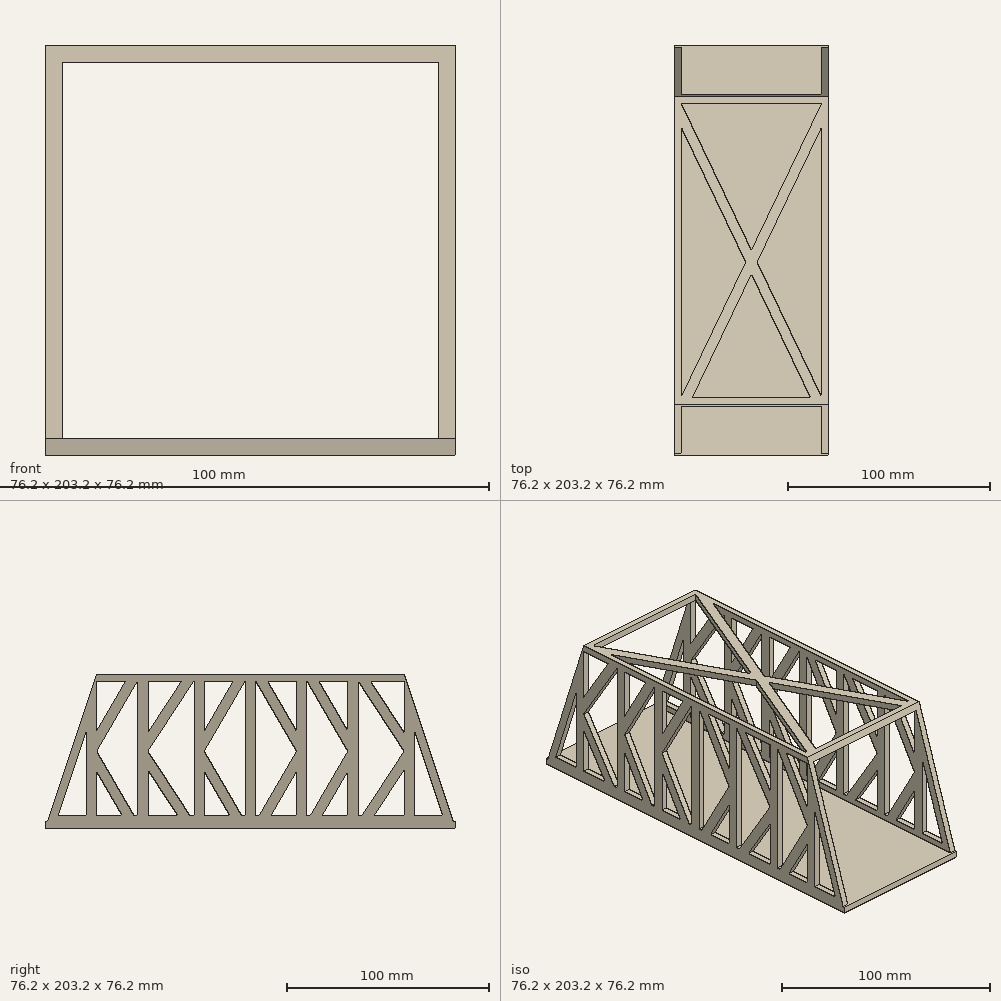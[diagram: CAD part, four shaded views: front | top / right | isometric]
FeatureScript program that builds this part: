
annotation { "Feature Type Name" : "Feature", "Feature Type Description" : "" }
export const myFeature = defineFeature(function(context is Context, id is Id, definition is map)
    precondition{}
    {
        {
            var Q0;
            Q0=qCreatedBy(makeId("Right.planeOp"),FACE);
            var sketch = newSketch(context, id + "F0", { "sketchPlane" : qUnion([Q0])});
            skLineSegment(sketch, "E0", {"start": v(-101.6, -38.1) * mm, "end": v(101.6, -38.1) * mm});
            skLineSegment(sketch, "E1", {"start": v(-76.2, 38.1) * mm, "end": v(76.2, 38.1) * mm});
            skLineSegment(sketch, "E2", {"start": v(-76.2, 38.1) * mm, "end": v(-101.6, -38.1) * mm});
            skLineSegment(sketch, "E3", {"start": v(76.2, 38.1) * mm, "end": v(101.6, -38.1) * mm});
            skSolve(sketch);
        }
        {
            var Q0;
            Q0 = qSketchRegion(id + "F0", true);
            extrude(context, id + "F1", {"entities" : qUnion([Q0]), "endBound" : BoundingType.SYMMETRIC, "depth" : 76.2 * mm, "offsetDistance" : 25.4 * mm});
        }
        {
            var Q0;
            Q0=qCreatedBy(makeId("Front.planeOp"),FACE);
            var sketch = newSketch(context, id + "F2", { "sketchPlane" : qUnion([Q0])});
            skLineSegment(sketch, "E4.bottom", {"start": v(34.92, -34.92) * mm, "end": v(-34.92, -34.93) * mm});
            skLineSegment(sketch, "E4.top", {"start": v(34.92, 34.93) * mm, "end": v(-34.92, 34.92) * mm});
            skLineSegment(sketch, "E4.left", {"start": v(-34.92, -34.92) * mm, "end": v(-34.92, 34.92) * mm});
            skLineSegment(sketch, "E4.right", {"start": v(34.92, -34.92) * mm, "end": v(34.92, 34.92) * mm});
            skPoint(sketch, "E4.middle", {"position": v(0, 0) * mm});
            skSolve(sketch);
        }
        {
            var Q0;
            Q0 = qSketchRegion(id + "F2", true);
            extrude(context, id + "F3", {"entities" : qUnion([Q0]), "operationType" : NewBodyOperationType.REMOVE, "endBound" : BoundingType.SYMMETRIC, "oppositeDirection" : true, "depth" : 254 * mm, "offsetDistance" : 25.4 * mm});
        }
        {
            var Q0;
            Q0=makeQuery(id+"F1.opExtrude","CAP_FACE",FACE,{"disambiguationData":[OSD([sQuery(id+"F0.wireOp",EDGE,"E0"),sQuery(id+"F0.wireOp",EDGE,"E1"),sQuery(id+"F0.wireOp",EDGE,"E2"),sQuery(id+"F0.wireOp",EDGE,"E3")])],"isStart":false});
            var sketch = newSketch(context, id + "F4", { "sketchPlane" : qUnion([Q0])});
            skLineSegment(sketch, "E5.bottom", {"start": v(76.2, -34.92) * mm, "end": v(-76.2, -34.92) * mm});
            skLineSegment(sketch, "E5.top", {"start": v(76.2, 34.92) * mm, "end": v(-76.2, 34.92) * mm});
            skLineSegment(sketch, "E5.left", {"start": v(76.2, -34.92) * mm, "end": v(76.2, 34.92) * mm});
            skLineSegment(sketch, "E5.right", {"start": v(-76.2, -34.92) * mm, "end": v(-76.2, 34.92) * mm});
            skPoint(sketch, "E5.middle", {"position": v(0, 0) * mm});
            skLineSegment(sketch, "E6.bottom", {"start": v(2.54, -34.92) * mm, "end": v(-2.54, -34.92) * mm});
            skLineSegment(sketch, "E6.top", {"start": v(2.54, 34.92) * mm, "end": v(-2.54, 34.92) * mm});
            skLineSegment(sketch, "E6.left", {"start": v(2.54, -34.93) * mm, "end": v(2.54, 34.93) * mm});
            skLineSegment(sketch, "E6.right", {"start": v(-2.54, -34.93) * mm, "end": v(-2.54, 34.93) * mm});
            skLineSegment(sketch, "E7.bottom", {"start": v(-50.8, -34.92) * mm, "end": v(-55.88, -34.92) * mm});
            skLineSegment(sketch, "E7.top", {"start": v(-50.8, 34.92) * mm, "end": v(-55.88, 34.92) * mm});
            skLineSegment(sketch, "E7.left", {"start": v(-50.8, -34.93) * mm, "end": v(-50.8, 34.93) * mm});
            skLineSegment(sketch, "E7.right", {"start": v(-55.88, -34.93) * mm, "end": v(-55.88, 34.93) * mm});
            skPoint(sketch, "E7.middle", {"position": v(-53.34, 0) * mm});
            skLineSegment(sketch, "E8.bottom", {"start": v(-22.86, -34.92) * mm, "end": v(-27.94, -34.92) * mm});
            skLineSegment(sketch, "E8.top", {"start": v(-22.86, 34.92) * mm, "end": v(-27.94, 34.92) * mm});
            skLineSegment(sketch, "E8.left", {"start": v(-22.86, -34.92) * mm, "end": v(-22.86, 34.92) * mm});
            skLineSegment(sketch, "E8.right", {"start": v(-27.94, -34.92) * mm, "end": v(-27.94, 34.92) * mm});
            skPoint(sketch, "E8.middle", {"position": v(-25.4, 0) * mm});
            skLineSegment(sketch, "E9.bottom", {"start": v(27.94, -34.92) * mm, "end": v(22.86, -34.92) * mm});
            skLineSegment(sketch, "E9.top", {"start": v(27.94, 34.92) * mm, "end": v(22.86, 34.92) * mm});
            skLineSegment(sketch, "E9.left", {"start": v(27.94, -34.92) * mm, "end": v(27.94, 34.92) * mm});
            skLineSegment(sketch, "E9.right", {"start": v(22.86, -34.93) * mm, "end": v(22.86, 34.92) * mm});
            skPoint(sketch, "E9.middle", {"position": v(25.4, 0) * mm});
            skLineSegment(sketch, "E10.bottom", {"start": v(53.34, -34.92) * mm, "end": v(48.26, -34.92) * mm});
            skLineSegment(sketch, "E10.top", {"start": v(53.34, 34.92) * mm, "end": v(48.26, 34.92) * mm});
            skLineSegment(sketch, "E10.left", {"start": v(53.34, -34.93) * mm, "end": v(53.34, 34.93) * mm});
            skLineSegment(sketch, "E10.right", {"start": v(48.26, -34.93) * mm, "end": v(48.26, 34.93) * mm});
            skPoint(sketch, "E10.middle", {"position": v(50.8, 0) * mm});
            skLineSegment(sketch, "E11", {"start": v(-55.88, 34.92) * mm, "end": v(-76.2, 0) * mm});
            skLineSegment(sketch, "E12", {"start": v(-76.2, 0) * mm, "end": v(-55.88, -34.92) * mm});
            skLineSegment(sketch, "E13", {"start": v(-27.94, 34.92) * mm, "end": v(-50.8, 0) * mm});
            skLineSegment(sketch, "E14", {"start": v(-50.8, 0) * mm, "end": v(-27.94, -34.92) * mm});
            skLineSegment(sketch, "E15", {"start": v(-2.54, 34.92) * mm, "end": v(-22.86, 0) * mm});
            skLineSegment(sketch, "E16", {"start": v(-22.86, 0) * mm, "end": v(-2.54, -34.92) * mm});
            skLineSegment(sketch, "E17", {"start": v(2.54, 34.92) * mm, "end": v(22.86, 0) * mm});
            skLineSegment(sketch, "E18", {"start": v(22.86, 0) * mm, "end": v(2.54, -34.92) * mm});
            skLineSegment(sketch, "E19", {"start": v(27.94, 34.93) * mm, "end": v(48.26, 0) * mm});
            skLineSegment(sketch, "E20", {"start": v(48.26, 0) * mm, "end": v(27.94, -34.93) * mm});
            skLineSegment(sketch, "E21", {"start": v(53.34, 34.92) * mm, "end": v(76.2, 0) * mm});
            skLineSegment(sketch, "E22", {"start": v(76.2, 0) * mm, "end": v(53.34, -34.92) * mm});
            skLineSegment(sketch, "E23", {"start": v(-76.2, -10.1) * mm, "end": v(-61.76, -34.93) * mm});
            skLineSegment(sketch, "E24", {"start": v(-34.01, 34.93) * mm, "end": v(-50.8, 9.28) * mm});
            skLineSegment(sketch, "E25", {"start": v(-50.8, -9.28) * mm, "end": v(-34.01, -34.93) * mm});
            skLineSegment(sketch, "E26", {"start": v(-8.42, 34.93) * mm, "end": v(-22.86, 10.1) * mm});
            skLineSegment(sketch, "E27", {"start": v(-22.86, -10.1) * mm, "end": v(-8.42, -34.93) * mm});
            skLineSegment(sketch, "E28", {"start": v(-61.76, 34.93) * mm, "end": v(-76.2, 10.1) * mm});
            skLineSegment(sketch, "E29", {"start": v(8.42, 34.93) * mm, "end": v(22.86, 10.1) * mm});
            skLineSegment(sketch, "E30", {"start": v(22.86, -10.1) * mm, "end": v(8.42, -34.93) * mm});
            skLineSegment(sketch, "E31", {"start": v(33.82, 34.93) * mm, "end": v(48.26, 10.1) * mm});
            skLineSegment(sketch, "E32", {"start": v(48.26, -10.1) * mm, "end": v(33.82, -34.93) * mm});
            skLineSegment(sketch, "E33", {"start": v(59.41, 34.93) * mm, "end": v(76.2, 9.28) * mm});
            skLineSegment(sketch, "E34", {"start": v(76.2, -9.28) * mm, "end": v(59.41, -34.93) * mm});
            skLineSegment(sketch, "E35", {"start": v(-81.28, -34.93) * mm, "end": v(-81.28, 10.1) * mm});
            skLineSegment(sketch, "E36", {"start": v(-81.28, 10.1) * mm, "end": v(-96.29, -34.93) * mm});
            skLineSegment(sketch, "E37", {"start": v(-96.29, -34.92) * mm, "end": v(-81.28, -34.92) * mm});
            skLineSegment(sketch, "E38.MirrorCS", {"start": v(81.28, -34.93) * mm, "end": v(81.28, 10.1) * mm});
            skLineSegment(sketch, "E39.MirrorCS", {"start": v(81.28, 10.1) * mm, "end": v(96.29, -34.93) * mm});
            skLineSegment(sketch, "E40.MirrorCS", {"start": v(96.29, -34.92) * mm, "end": v(81.28, -34.92) * mm});
            skSolve(sketch);
        }
        {
            var Q0;
            Q0=makeQuery(id+"F4.imprint","IMPRINT",FACE,{"disambiguationData":[TD([[makeQuery(id+"F4.imprint","IMPRINT",EDGE,{"derivedFrom":sQuery(id+"F4.wireOp",EDGE,"E35")}),1.0]])]});
            var Q1;
            {var subQ3=sQuery(id+"F4.wireOp",EDGE,"E28");Q1=makeQuery(id+"F4.imprint","IMPRINT",FACE,{"disambiguationData":[TD([[makeQuery(id+"F4.imprint","IMPRINT",EDGE,{"derivedFrom":subQ3}),-1.0]])]});}
            var Q2;
            Q2=makeQuery(id+"F4.imprint","IMPRINT",FACE,{"disambiguationData":[TD([[makeQuery(id+"F4.imprint","IMPRINT",EDGE,{"derivedFrom":sQuery(id+"F4.wireOp",EDGE,"E7.right")}),1.0]])]});
            var Q3;
            {var subQ3=sQuery(id+"F4.wireOp",EDGE,"E23");Q3=makeQuery(id+"F4.imprint","IMPRINT",FACE,{"disambiguationData":[TD([[makeQuery(id+"F4.imprint","IMPRINT",EDGE,{"derivedFrom":subQ3}),-1.0]])]});}
            var Q4;
            {var subQ3=sQuery(id+"F4.wireOp",EDGE,"E24");Q4=makeQuery(id+"F4.imprint","IMPRINT",FACE,{"disambiguationData":[TD([[makeQuery(id+"F4.imprint","IMPRINT",EDGE,{"derivedFrom":subQ3}),-1.0]])]});}
            var Q5;
            Q5=makeQuery(id+"F4.imprint","IMPRINT",FACE,{"disambiguationData":[TD([[makeQuery(id+"F4.imprint","IMPRINT",EDGE,{"derivedFrom":sQuery(id+"F4.wireOp",EDGE,"E8.right")}),1.0]])]});
            var Q6;
            {var subQ3=sQuery(id+"F4.wireOp",EDGE,"E25");Q6=makeQuery(id+"F4.imprint","IMPRINT",FACE,{"disambiguationData":[TD([[makeQuery(id+"F4.imprint","IMPRINT",EDGE,{"derivedFrom":subQ3}),-1.0]])]});}
            var Q7;
            {var subQ3=sQuery(id+"F4.wireOp",EDGE,"E26");Q7=makeQuery(id+"F4.imprint","IMPRINT",FACE,{"disambiguationData":[TD([[makeQuery(id+"F4.imprint","IMPRINT",EDGE,{"derivedFrom":subQ3}),-1.0]])]});}
            var Q8;
            Q8=makeQuery(id+"F4.imprint","IMPRINT",FACE,{"disambiguationData":[TD([[makeQuery(id+"F4.imprint","IMPRINT",EDGE,{"derivedFrom":sQuery(id+"F4.wireOp",EDGE,"E6.right")}),1.0]])]});
            var Q9;
            {var subQ3=sQuery(id+"F4.wireOp",EDGE,"E27");Q9=makeQuery(id+"F4.imprint","IMPRINT",FACE,{"disambiguationData":[TD([[makeQuery(id+"F4.imprint","IMPRINT",EDGE,{"derivedFrom":subQ3}),-1.0]])]});}
            var Q10;
            Q10=makeQuery(id+"F4.imprint","IMPRINT",FACE,{"disambiguationData":[TD([[makeQuery(id+"F4.imprint","IMPRINT",EDGE,{"derivedFrom":sQuery(id+"F4.wireOp",EDGE,"E6.left")}),-1.0]])]});
            var Q11;
            {var subQ3=sQuery(id+"F4.wireOp",EDGE,"E29");Q11=makeQuery(id+"F4.imprint","IMPRINT",FACE,{"disambiguationData":[TD([[makeQuery(id+"F4.imprint","IMPRINT",EDGE,{"derivedFrom":subQ3}),1.0]])]});}
            var Q12;
            Q12=makeQuery(id+"F4.imprint","IMPRINT",FACE,{"disambiguationData":[TD([[makeQuery(id+"F4.imprint","IMPRINT",EDGE,{"derivedFrom":sQuery(id+"F4.wireOp",EDGE,"E9.left")}),-1.0]])]});
            var Q13;
            {var subQ3=sQuery(id+"F4.wireOp",EDGE,"E30");Q13=makeQuery(id+"F4.imprint","IMPRINT",FACE,{"disambiguationData":[TD([[makeQuery(id+"F4.imprint","IMPRINT",EDGE,{"derivedFrom":subQ3}),1.0]])]});}
            var Q14;
            {var subQ3=sQuery(id+"F4.wireOp",EDGE,"E31");Q14=makeQuery(id+"F4.imprint","IMPRINT",FACE,{"disambiguationData":[TD([[makeQuery(id+"F4.imprint","IMPRINT",EDGE,{"derivedFrom":subQ3}),1.0]])]});}
            var Q15;
            {var subQ3=sQuery(id+"F4.wireOp",EDGE,"E32");Q15=makeQuery(id+"F4.imprint","IMPRINT",FACE,{"disambiguationData":[TD([[makeQuery(id+"F4.imprint","IMPRINT",EDGE,{"derivedFrom":subQ3}),1.0]])]});}
            var Q16;
            Q16=makeQuery(id+"F4.imprint","IMPRINT",FACE,{"disambiguationData":[TD([[makeQuery(id+"F4.imprint","IMPRINT",EDGE,{"derivedFrom":sQuery(id+"F4.wireOp",EDGE,"E10.left")}),-1.0]])]});
            var Q17;
            {var subQ3=sQuery(id+"F4.wireOp",EDGE,"E33");Q17=makeQuery(id+"F4.imprint","IMPRINT",FACE,{"disambiguationData":[TD([[makeQuery(id+"F4.imprint","IMPRINT",EDGE,{"derivedFrom":subQ3}),1.0]])]});}
            var Q18;
            {var subQ3=sQuery(id+"F4.wireOp",EDGE,"E34");Q18=makeQuery(id+"F4.imprint","IMPRINT",FACE,{"disambiguationData":[TD([[makeQuery(id+"F4.imprint","IMPRINT",EDGE,{"derivedFrom":subQ3}),1.0]])]});}
            var Q19;
            Q19=makeQuery(id+"F4.imprint","IMPRINT",FACE,{"disambiguationData":[TD([[makeQuery(id+"F4.imprint","IMPRINT",EDGE,{"derivedFrom":sQuery(id+"F4.wireOp",EDGE,"E38.MirrorCS")}),-1.0]])]});
            extrude(context, id + "F5", {"entities" : qUnion([Q0, Q1, Q2, Q3, Q4, Q5, Q6, Q7, Q8, Q9, Q10, Q11, Q12, Q13, Q14, Q15, Q16, Q17, Q18, Q19]), "operationType" : NewBodyOperationType.REMOVE, "oppositeDirection" : true, "depth" : 76.2 * mm, "offsetDistance" : 25.4 * mm});
        }
        {
            var Q0;
            Q0=makeQuery(id+"F1.opExtrude","CAP_FACE",FACE,{"disambiguationData":[OSD([sQuery(id+"F0.wireOp",EDGE,"E0"),sQuery(id+"F0.wireOp",EDGE,"E1"),sQuery(id+"F0.wireOp",EDGE,"E2"),sQuery(id+"F0.wireOp",EDGE,"E3")])],"isStart":false});
            var sketch = newSketch(context, id + "F6", { "sketchPlane" : qUnion([Q0])});
            skLineSegment(sketch, "E41.bottom", {"start": v(-96.29, -34.93) * mm, "end": v(-101.6, -34.93) * mm});
            skLineSegment(sketch, "E41.top", {"start": v(-96.29, -38.1) * mm, "end": v(-101.6, -38.1) * mm});
            skLineSegment(sketch, "E41.left", {"start": v(-96.29, -34.93) * mm, "end": v(-96.29, -38.1) * mm});
            skLineSegment(sketch, "E41.right", {"start": v(-101.6, -34.93) * mm, "end": v(-101.6, -38.1) * mm});
            skLineSegment(sketch, "E42.MirrorCS", {"start": v(96.29, -34.93) * mm, "end": v(101.6, -34.93) * mm});
            skLineSegment(sketch, "E43.MirrorCS", {"start": v(101.6, -34.93) * mm, "end": v(101.6, -38.1) * mm});
            skLineSegment(sketch, "E44.MirrorCS", {"start": v(96.29, -34.93) * mm, "end": v(96.29, -38.1) * mm});
            skLineSegment(sketch, "E45.MirrorCS", {"start": v(96.29, -38.1) * mm, "end": v(101.6, -38.1) * mm});
            skSolve(sketch);
        }
        {
            var Q0;
            Q0 = qSketchRegion(id + "F6", true);
            extrude(context, id + "F7", {"entities" : qUnion([Q0]), "operationType" : NewBodyOperationType.ADD, "oppositeDirection" : true, "depth" : 76.2 * mm, "offsetDistance" : 25.4 * mm});
        }
        {
            var Q0;
            Q0=makeQuery(id+"F1.opExtrude","SWEPT_FACE",FACE,{"disambiguationData":[OSD([sQuery(id+"F0.wireOp",EDGE,"E1")])]});
            var sketch = newSketch(context, id + "F8", { "sketchPlane" : qUnion([Q0])});
            skLineSegment(sketch, "E46.bottom", {"start": v(34.92, -73.03) * mm, "end": v(-34.93, -73.03) * mm});
            skLineSegment(sketch, "E46.top", {"start": v(34.92, 73.03) * mm, "end": v(-34.93, 73.03) * mm});
            skLineSegment(sketch, "E46.left", {"start": v(34.92, -73.03) * mm, "end": v(34.92, 73.03) * mm});
            skLineSegment(sketch, "E46.right", {"start": v(-34.92, -73.03) * mm, "end": v(-34.92, 73.03) * mm});
            skPoint(sketch, "E46.middle", {"position": v(0, 0) * mm});
            skLineSegment(sketch, "E47", {"start": v(-34.92, 73.03) * mm, "end": v(34.92, -73.03) * mm});
            skLineSegment(sketch, "E48", {"start": v(-34.92, -73.03) * mm, "end": v(34.92, 73.03) * mm});
            skLineSegment(sketch, "E49", {"start": v(-34.92, 61.25) * mm, "end": v(29.3, -73.03) * mm});
            skLineSegment(sketch, "E50", {"start": v(34.92, 61.25) * mm, "end": v(-29.3, -73.03) * mm});
            skSolve(sketch);
        }
        {
            var Q0;
            {var subQ1=sQuery(id+"F8.wireOp",EDGE,"E46.right");var subQ3=sQuery(id+"F8.wireOp",EDGE,"E49");var subQ4=makeQuery(id+"F8.imprint","INTERSECT",VERTEX,{"derivedFrom":[subQ1,subQ3]});Q0=makeQuery(id+"F8.imprint","IMPRINT",FACE,{"disambiguationData":[TD([[makeQuery(id+"F8.imprint","IMPRINT",EDGE,{"disambiguationData":[TD([[subQ4,-1.0]])],"derivedFrom":subQ3}),-1.0]])]});}
            var Q1;
            {var subQ0=sQuery(id+"F8.wireOp",EDGE,"E46.top");Q1=makeQuery(id+"F8.imprint","IMPRINT",FACE,{"disambiguationData":[TD([[makeQuery(id+"F8.imprint","IMPRINT",EDGE,{"derivedFrom":subQ0}),1.0]])]});}
            var Q2;
            {var subQ1=sQuery(id+"F8.wireOp",EDGE,"E46.left");var subQ3=sQuery(id+"F8.wireOp",EDGE,"E50");var subQ4=makeQuery(id+"F8.imprint","INTERSECT",VERTEX,{"derivedFrom":[subQ1,subQ3]});Q2=makeQuery(id+"F8.imprint","IMPRINT",FACE,{"disambiguationData":[TD([[makeQuery(id+"F8.imprint","IMPRINT",EDGE,{"disambiguationData":[TD([[subQ4,-1.0]])],"derivedFrom":subQ3}),1.0]])]});}
            var Q3;
            {var subQ0=sQuery(id+"F8.wireOp",EDGE,"E49");var subQ1=sQuery(id+"F8.wireOp",EDGE,"E46.bottom");var subQ2=makeQuery(id+"F8.imprint","INTERSECT",VERTEX,{"derivedFrom":[subQ1,subQ0]});Q3=makeQuery(id+"F8.imprint","IMPRINT",FACE,{"disambiguationData":[TD([[makeQuery(id+"F8.imprint","IMPRINT",EDGE,{"disambiguationData":[TD([[subQ2,-1.0]])],"derivedFrom":subQ1}),-1.0]])]});}
            extrude(context, id + "F9", {"entities" : qUnion([Q0, Q1, Q2, Q3]), "operationType" : NewBodyOperationType.REMOVE, "oppositeDirection" : true, "depth" : 3.17 * mm, "offsetDistance" : 25.4 * mm});
        }
        {
            var Q0;
            {var subQ0=sQuery(id+"F4.wireOp",EDGE,"E5.bottom");Q0=makeQuery(id+"F7.boolean.opBoolean","MERGE",FACE,{"derivedFrom":[makeQuery(id+"F5.boolean.opBoolean","MERGE",FACE,{"derivedFrom":[makeQuery(id+"F3.boolean.opBoolean","COPY",FACE,{"derivedFrom":makeQuery(id+"F3.opExtrude","SWEPT_FACE",FACE,{"disambiguationData":[OSD([sQuery(id+"F2.wireOp",EDGE,"E4.bottom")])]})})],"fromTools":[makeQuery(id+"F5.opExtrude","SWEPT_FACE",FACE,{"disambiguationData":[OSD([subQ0]),TDD([makeQuery(id+"F4.imprint","IMPRINT",EDGE,{"disambiguationData":[TD([[makeQuery(id+"F4.imprint","INTERSECT",VERTEX,{"derivedFrom":[subQ0,sQuery(id+"F4.wireOp",EDGE,"E5.left")]}),-1.0]])],"derivedFrom":subQ0})])]}),makeQuery(id+"F5.opExtrude","SWEPT_FACE",FACE,{"disambiguationData":[OSD([subQ0]),TDD([makeQuery(id+"F4.imprint","IMPRINT",EDGE,{"disambiguationData":[TD([[makeQuery(id+"F4.imprint","INTERSECT",VERTEX,{"derivedFrom":[subQ0,sQuery(id+"F4.wireOp",EDGE,"E32")]}),1.0]])],"derivedFrom":subQ0})])]}),makeQuery(id+"F5.opExtrude","SWEPT_FACE",FACE,{"disambiguationData":[OSD([subQ0]),TDD([makeQuery(id+"F4.imprint","IMPRINT",EDGE,{"disambiguationData":[TD([[makeQuery(id+"F4.imprint","INTERSECT",VERTEX,{"derivedFrom":[subQ0,sQuery(id+"F4.wireOp",EDGE,"E30")]}),1.0]])],"derivedFrom":subQ0})])]}),makeQuery(id+"F5.opExtrude","SWEPT_FACE",FACE,{"disambiguationData":[OSD([subQ0]),TDD([makeQuery(id+"F4.imprint","IMPRINT",EDGE,{"disambiguationData":[TD([[makeQuery(id+"F4.imprint","INTERSECT",VERTEX,{"derivedFrom":[subQ0,sQuery(id+"F4.wireOp",EDGE,"E27")]}),-1.0]])],"derivedFrom":subQ0})])]}),makeQuery(id+"F5.opExtrude","SWEPT_FACE",FACE,{"disambiguationData":[OSD([subQ0]),TDD([makeQuery(id+"F4.imprint","IMPRINT",EDGE,{"disambiguationData":[TD([[makeQuery(id+"F4.imprint","INTERSECT",VERTEX,{"derivedFrom":[subQ0,sQuery(id+"F4.wireOp",EDGE,"E25")]}),-1.0]])],"derivedFrom":subQ0})])]}),makeQuery(id+"F5.opExtrude","SWEPT_FACE",FACE,{"disambiguationData":[OSD([subQ0]),TDD([makeQuery(id+"F4.imprint","IMPRINT",EDGE,{"disambiguationData":[TD([[makeQuery(id+"F4.imprint","INTERSECT",VERTEX,{"derivedFrom":[subQ0,sQuery(id+"F4.wireOp",EDGE,"E5.right")]}),1.0]])],"derivedFrom":subQ0})])]}),makeQuery(id+"F5.opExtrude","SWEPT_FACE",FACE,{"disambiguationData":[OSD([sQuery(id+"F4.wireOp",EDGE,"E37")])]}),makeQuery(id+"F5.opExtrude","SWEPT_FACE",FACE,{"disambiguationData":[OSD([sQuery(id+"F4.wireOp",EDGE,"E40.MirrorCS")])]})]}),makeQuery(id+"F7.opExtrude","SWEPT_FACE",FACE,{"disambiguationData":[OSD([sQuery(id+"F6.wireOp",EDGE,"E41.bottom")])]}),makeQuery(id+"F7.opExtrude","SWEPT_FACE",FACE,{"disambiguationData":[OSD([sQuery(id+"F6.wireOp",EDGE,"E42.MirrorCS")])]})]});}
            var sketch = newSketch(context, id + "F10", { "sketchPlane" : qUnion([Q0])});
            skLineSegment(sketch, "E51.bottom", {"start": v(34.92, 96.29) * mm, "end": v(38.1, 96.29) * mm});
            skLineSegment(sketch, "E51.top", {"start": v(34.92, -96.29) * mm, "end": v(38.1, -96.29) * mm});
            skLineSegment(sketch, "E51.left", {"start": v(34.92, 96.29) * mm, "end": v(34.92, -96.29) * mm});
            skLineSegment(sketch, "E51.right", {"start": v(38.1, 96.29) * mm, "end": v(38.1, -96.29) * mm});
            skLineSegment(sketch, "E52.MirrorCS", {"start": v(-38.1, 96.29) * mm, "end": v(-38.1, -96.29) * mm});
            skLineSegment(sketch, "E53.MirrorCS", {"start": v(-34.92, 96.29) * mm, "end": v(-34.92, -96.29) * mm});
            skLineSegment(sketch, "E54", {"start": v(-38.1, -96.29) * mm, "end": v(-34.92, -96.29) * mm});
            skLineSegment(sketch, "E55", {"start": v(-38.1, 96.29) * mm, "end": v(-34.92, 96.29) * mm});
            skSolve(sketch);
        }
        {
            var Q0;
            Q0 = qSketchRegion(id + "F10", true);
            extrude(context, id + "F11", {"entities" : qUnion([Q0]), "operationType" : NewBodyOperationType.ADD, "depth" : 3.17 * mm, "offsetDistance" : 25.4 * mm});
        }
    });
